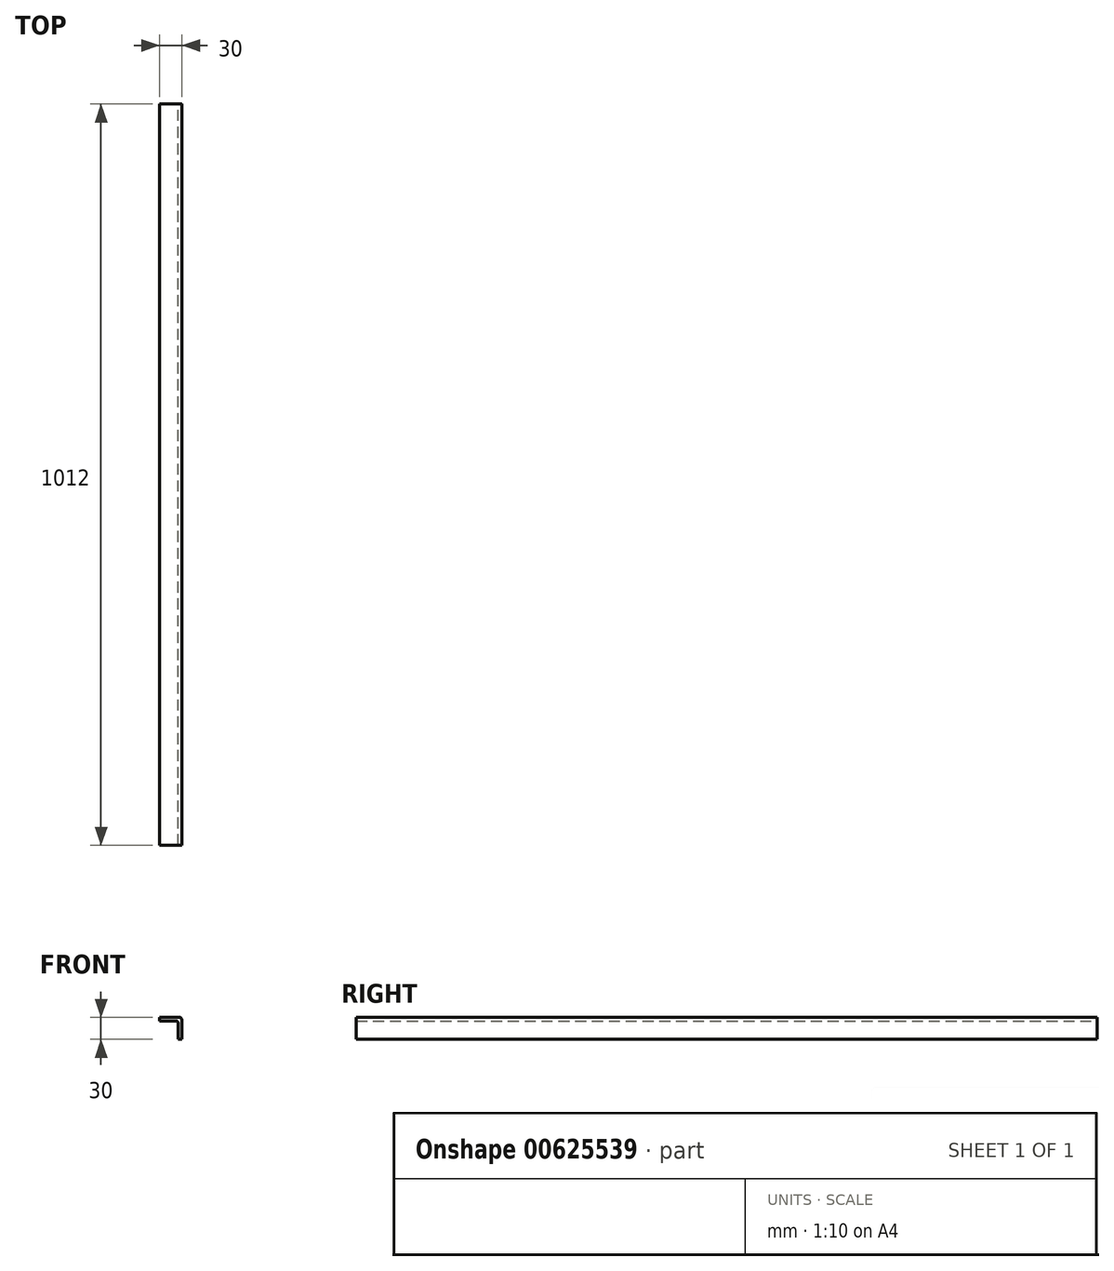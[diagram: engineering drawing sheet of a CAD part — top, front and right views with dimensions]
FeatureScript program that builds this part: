
annotation { "Feature Type Name" : "Feature", "Feature Type Description" : "" }
export const myFeature = defineFeature(function(context is Context, id is Id, definition is map)
    precondition{}
    {
        {
            var Q0;
            Q0=qCreatedBy(makeId("Front.planeOp"),FACE);
            var sketch = newSketch(context, id + "F0", { "sketchPlane" : qUnion([Q0])});
            skLineSegment(sketch, "E0.bottom", {"start": v(-15, 15) * mm, "end": v(12.5, 15) * mm});
            skLineSegment(sketch, "E0.top", {"start": v(10, -15) * mm, "end": v(15, -15) * mm});
            skLineSegment(sketch, "E0.left", {"start": v(-15, 15) * mm, "end": v(-15, 10) * mm});
            skLineSegment(sketch, "E0.right", {"start": v(15, 12.5) * mm, "end": v(15, -15) * mm});
            skPoint(sketch, "E0.middle", {"position": v(0, 0) * mm});
            skLineSegment(sketch, "E1", {"start": v(-15, 10) * mm, "end": v(7.5, 10) * mm});
            skLineSegment(sketch, "E2", {"start": v(10, 7.5) * mm, "end": v(10, -15) * mm});
            skPoint(sketch, "E3.orphan", {"position": v(-15, -15) * mm});
            skPoint(sketch, "E4.visualSharp", {"position": v(15, 15) * mm});
            skArc(sketch, "E4.filletArc", {"start": v(15, 12.5) * mm, "mid": v(14.27, 14.27) * mm, "end": v(12.5, 15) * mm});
            skPoint(sketch, "E5.visualSharp", {"position": v(10, 10) * mm});
            skArc(sketch, "E5.filletArc", {"start": v(10, 7.5) * mm, "mid": v(9.27, 9.27) * mm, "end": v(7.5, 10) * mm});
            skSolve(sketch);
        }
        {
            var Q0;
            Q0 = qSketchRegion(id + "F0", true);
            extrude(context, id + "F1", {"entities" : qUnion([Q0]), "depth" : 1012 * mm, "offsetDistance" : 25 * mm});
        }
    });
